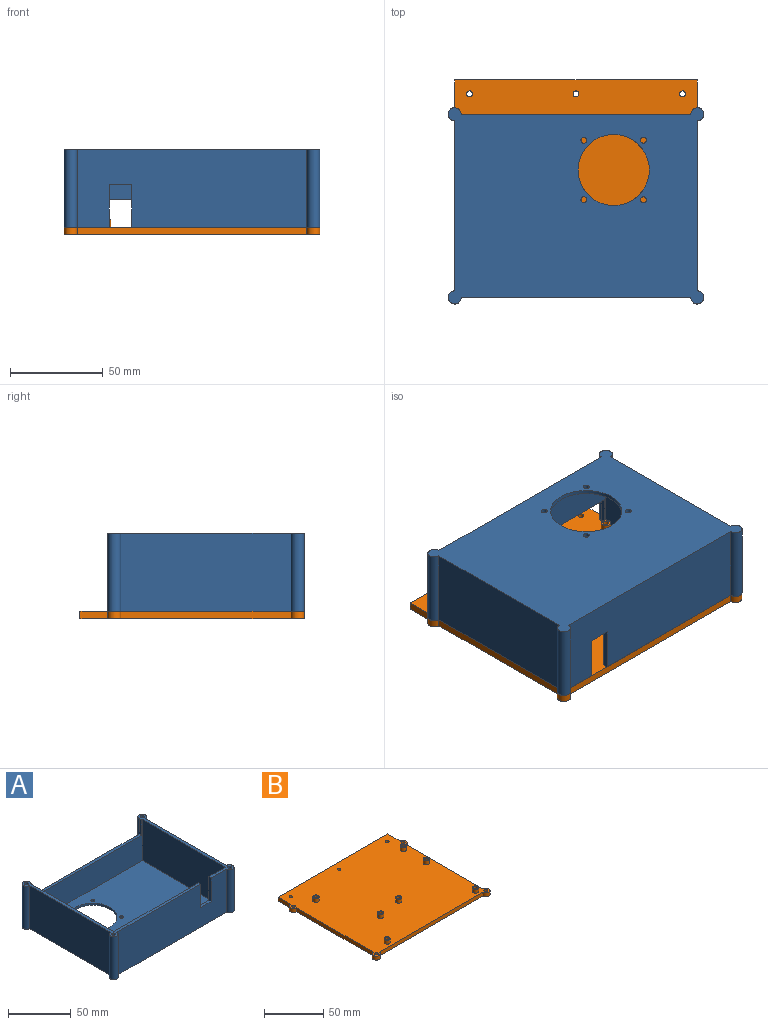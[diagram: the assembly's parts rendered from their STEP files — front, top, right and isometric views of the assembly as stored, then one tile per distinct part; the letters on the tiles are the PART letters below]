
ASSEMBLY  parts=2 mates=1
PART A: 35 faces, bbox 137.5x105.5x42 mm
  f0: plane 105.5x24.3mm, normal (0,0,1), area 336.1mm2, adj f2,f4,f5,f6,f7,f10,f12,f16
  f1: plane 123.5x27mm, normal (0,1,0), area 3334.5mm2, adj f7,f8,f18,f26
  f2: plane 125.5x40mm, normal (0,-1,0), area 3167.5mm2, adj f0,f3,f11,f16,f18,f19,f20,f25
  f3: plane 105.5x101.2mm, normal (0,0,1), area 528.4mm2, adj f2,f4,f8,f9,f10,f11,f13,f14
  f4: plane 123.5x42mm, normal (0,-1,0), area 4911mm2, adj f0,f3,f5,f15,f26,f32,f33,f34
  f5: cylinder r=3.5mm len=42mm, axis (0,0,-1), area 692.7mm2, adj f0,f4,f6,f26
  f6: plane 91.5x42mm, normal (1,0,0), area 3843mm2, adj f0,f5,f7,f26
  f7: cylinder r=3.5mm len=42mm, axis (0,0,-1), area 692.7mm2, adj f0,f1,f6,f20,f26
  f8: cylinder r=3.5mm len=42mm, axis (0,0,-1), area 692.7mm2, adj f1,f3,f9,f19,f26
  f9: plane 91.5x42mm, normal (-1,0,0), area 3843mm2, adj f3,f8,f15,f26
  f10: plane 125.5x40mm, normal (0,1,0), area 4744mm2, adj f0,f3,f11,f16,f25,f32,f33,f34
  f11: plane 93.5x40mm, normal (1,0,0), area 3740mm2, adj f2,f3,f10,f25
  f12: cylinder r=1.6mm len=40mm, axis (0,0,-1), area 402.1mm2, adj f0,f22
  f13: cylinder r=1.6mm len=40mm, axis (0,0,-1), area 402.1mm2, adj f3,f23
  f14: cylinder r=1.6mm len=40mm, axis (0,0,-1), area 402.1mm2, adj f3,f24
  f15: cylinder r=3.5mm len=42mm, axis (0,0,-1), area 692.7mm2, adj f3,f4,f9,f26
  f16: plane 93.5x40mm, normal (-1,0,0), area 3740mm2, adj f0,f2,f10,f25
  f17: cylinder r=1.6mm len=40mm, axis (0,0,-1), area 402.1mm2, adj f0,f21
  f18: plane 123.5x2.5mm, normal (0,0,1), area 308.8mm2, adj f1,f2,f19,f20
  f19: plane 15x2.5mm, normal (1,0,0), area 37.5mm2, adj f2,f3,f8,f18
  f20: plane 15x2.5mm, normal (-1,0,0), area 37.5mm2, adj f0,f2,f7,f18
  f21: plane 3.2x3.2mm, normal (0,0,1), area 8mm2, adj f17
  f22: plane 3.2x3.2mm, normal (0,0,1), area 8mm2, adj f12
  f23: plane 3.2x3.2mm, normal (0,0,1), area 8mm2, adj f13
  f24: plane 3.2x3.2mm, normal (0,0,1), area 8mm2, adj f14
  f25: plane 125.5x93.5mm, normal (0,0,1), area 10550mm2, adj f2,f10,f11,f16,f27,f28,f29,f30
  f26: plane 137.5x105.5mm, normal (0,0,-1), area 11785.4mm2, adj f1,f4,f5,f6,f7,f8,f9,f15
  f27: cylinder r=1.6mm len=3.2mm, axis (0,0,-1), area 20.1mm2, adj f25,f26
  f28: cylinder r=1.6mm len=3.2mm, axis (0,0,-1), area 20.1mm2, adj f25,f26
  f29: cylinder r=1.6mm len=3.2mm, axis (0,0,-1), area 20.1mm2, adj f25,f26
  f30: cylinder r=19.15mm len=38.3mm, axis (0,0,-1), area 240.6mm2, adj f25,f26
  f31: cylinder r=1.6mm len=3.2mm, axis (0,0,-1), area 20.1mm2, adj f25,f26
  f32: plane 23x2.5mm, normal (1,0,0), area 57.5mm2, adj f3,f4,f10,f33
  f33: plane 12x2.5mm, normal (0,0,1), area 30mm2, adj f4,f10,f32,f34
  f34: plane 23x2.5mm, normal (-1,0,0), area 57.5mm2, adj f0,f4,f10,f33
PART B: 40 faces, bbox 137.5x120.5x8 mm
  f0: cylinder r=1.6mm len=8mm, axis (0,0,-1), area 80.4mm2, adj f8,f39
  f1: cylinder r=1.6mm len=8mm, axis (0,0,-1), area 80.4mm2, adj f8,f31
  f2: cylinder r=1.6mm len=8mm, axis (0,0,-1), area 80.4mm2, adj f8,f29
  f3: cylinder r=1.6mm len=8mm, axis (0,0,-1), area 80.4mm2, adj f8,f37
  f4: cylinder r=1.6mm len=8mm, axis (0,0,-1), area 80.4mm2, adj f8,f33
  f5: cylinder r=1.6mm len=8mm, axis (0,0,-1), area 80.4mm2, adj f8,f27
  f6: cylinder r=1.6mm len=8mm, axis (0,0,-1), area 80.4mm2, adj f8,f35
  f7: plane 137.5x120.5mm, normal (0,0,1), area 15159.8mm2, adj f9,f10,f11,f12,f13,f14,f15,f16
  f8: plane 137.5x120.5mm, normal (0,0,-1), area 15252.1mm2, adj f0,f1,f2,f3,f4,f5,f6,f9
  f9: cylinder r=3.5mm len=7mm, axis (0,0,-1), area 44mm2, adj f7,f8,f10,f16
  f10: plane 15x4mm, normal (1,0,0), area 60mm2, adj f7,f8,f9,f11
  f11: plane 130.5x4mm, normal (0,1,0), area 522mm2, adj f7,f8,f10,f12
  f12: plane 15x4mm, normal (-1,0,0), area 60mm2, adj f7,f8,f11,f13
  f13: cylinder r=3.5mm len=7mm, axis (0,0,-1), area 44mm2, adj f7,f8,f12,f14
  f14: plane 91.5x4mm, normal (-1,0,0), area 366mm2, adj f7,f8,f13,f15
  f15: cylinder r=3.5mm len=7mm, axis (0,0,-1), area 66mm2, adj f7,f8,f14,f18
  f16: plane 91.5x4mm, normal (1,0,0), area 366mm2, adj f7,f8,f9,f19
  f17: cylinder r=1.6mm len=4mm, axis (0,0,-1), area 40.2mm2, adj f7,f8
  f18: plane 123.5x4mm, normal (0,-1,0), area 494mm2, adj f7,f8,f15,f19
  f19: cylinder r=3.5mm len=7mm, axis (0,0,-1), area 66mm2, adj f7,f8,f16,f18
  f20: cylinder r=1.6mm len=4mm, axis (0,0,-1), area 40.2mm2, adj f7,f8
  f21: cylinder r=1.6mm len=4mm, axis (0,0,-1), area 40.2mm2, adj f7,f8
  f22: cylinder r=1.6mm len=4mm, axis (0,0,-1), area 40.2mm2, adj f7,f8
  f23: cylinder r=1.6mm len=4mm, axis (0,0,-1), area 40.2mm2, adj f7,f8
  f24: cylinder r=1.6mm len=4mm, axis (0,0,-1), area 40.2mm2, adj f7,f8
  f25: cylinder r=1.6mm len=4mm, axis (0,0,-1), area 40.2mm2, adj f7,f8
  f26: cylinder r=2.6mm len=5.2mm, axis (0,0,-1), area 65.3mm2, adj f7,f27
  f27: plane 5.2x5.2mm, normal (0,0,1), area 13.2mm2, adj f5,f26
  f28: cylinder r=2.6mm len=5.2mm, axis (0,0,-1), area 65.3mm2, adj f7,f29
  f29: plane 5.2x5.2mm, normal (0,0,1), area 13.2mm2, adj f2,f28
  f30: cylinder r=2.6mm len=5.2mm, axis (0,0,-1), area 65.3mm2, adj f7,f31
  f31: plane 5.2x5.2mm, normal (0,0,1), area 13.2mm2, adj f1,f30
  f32: cylinder r=2.6mm len=5.2mm, axis (0,0,-1), area 65.3mm2, adj f7,f33
  f33: plane 5.2x5.2mm, normal (0,0,1), area 13.2mm2, adj f4,f32
  f34: cylinder r=2.6mm len=5.2mm, axis (0,0,-1), area 65.3mm2, adj f7,f35
  f35: plane 5.2x5.2mm, normal (0,0,1), area 13.2mm2, adj f6,f34
  f36: cylinder r=2.6mm len=5.2mm, axis (0,0,-1), area 65.3mm2, adj f7,f37
  f37: plane 5.2x5.2mm, normal (0,0,1), area 13.2mm2, adj f3,f36
  f38: cylinder r=2.6mm len=5.2mm, axis (0,0,-1), area 65.3mm2, adj f7,f39
  f39: plane 5.2x5.2mm, normal (0,0,1), area 13.2mm2, adj f0,f38
PLACE A rot(axis=(0,1,0),180deg) t=(12.96,0,58)mm
PLACE B t=(0,0,-15)mm
MATE fastened A.f7 <-> B.f13  axis (0,0,-1) through (-58.77,69.59,-11)mm
